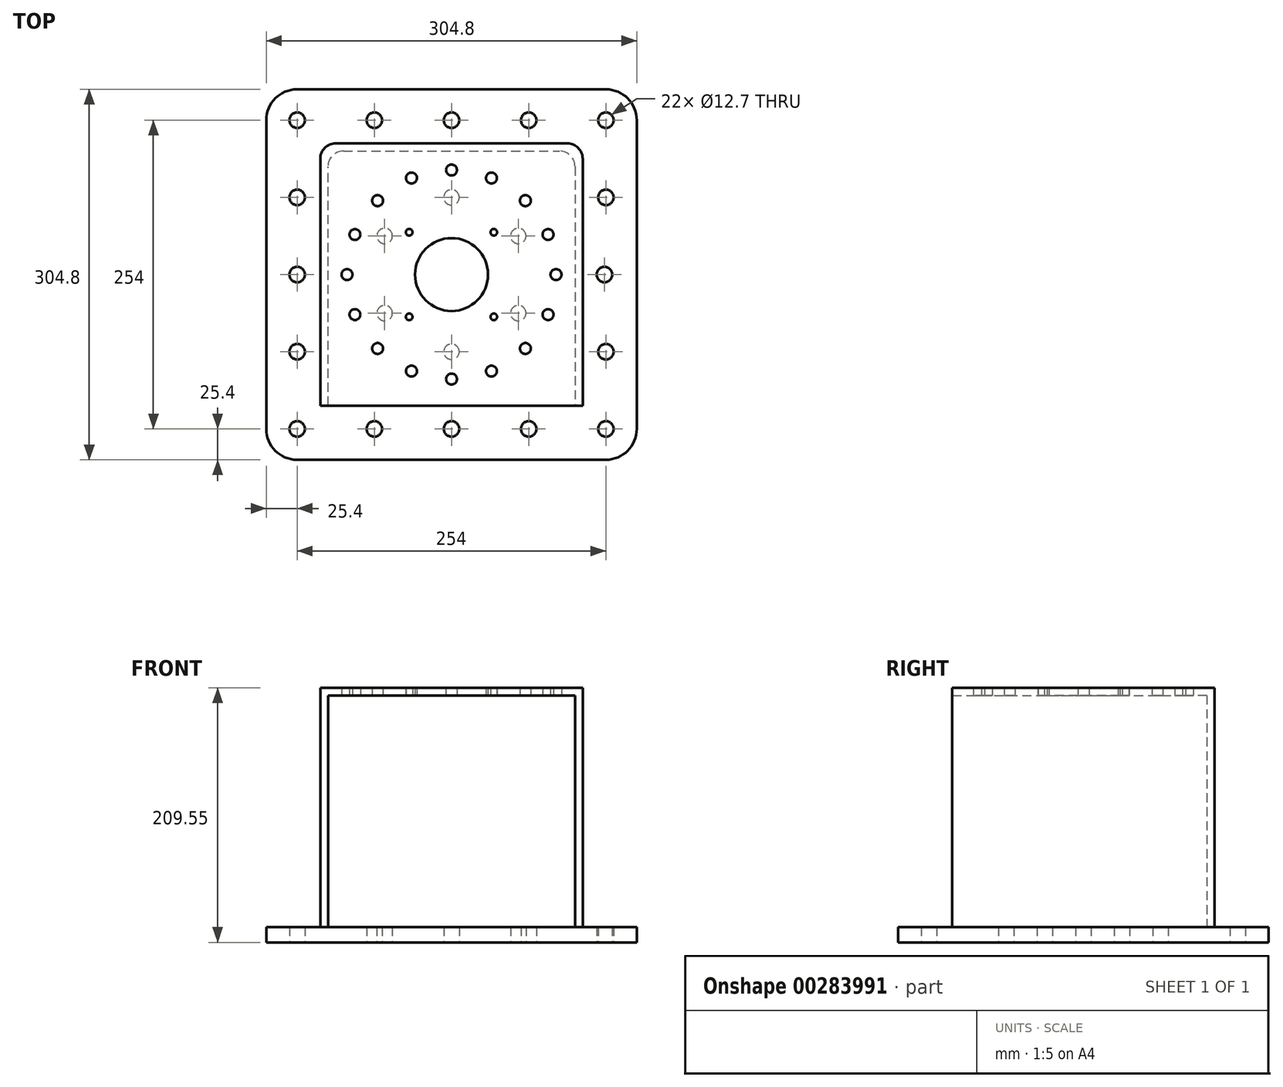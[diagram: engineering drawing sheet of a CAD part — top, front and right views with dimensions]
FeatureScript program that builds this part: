
annotation { "Feature Type Name" : "Feature", "Feature Type Description" : "" }
export const myFeature = defineFeature(function(context is Context, id is Id, definition is map)
    precondition{}
    {
        {
            var Q0;
            Q0=qCreatedBy(makeId("Top.planeOp"),FACE);
            var sketch = newSketch(context, id + "F0", { "sketchPlane" : qUnion([Q0])});
            skLineSegment(sketch, "E0.bottom", {"start": v(127, -152.4) * mm, "end": v(-127, -152.4) * mm});
            skLineSegment(sketch, "E0.top", {"start": v(127, 152.4) * mm, "end": v(-127, 152.4) * mm});
            skLineSegment(sketch, "E0.left", {"start": v(152.4, -127) * mm, "end": v(152.4, 127) * mm});
            skLineSegment(sketch, "E0.right", {"start": v(-152.4, -127) * mm, "end": v(-152.4, 127) * mm});
            skPoint(sketch, "E1.visualSharp", {"position": v(-152.4, 152.4) * mm});
            skArc(sketch, "E1.filletArc", {"start": v(-127, 152.4) * mm, "mid": v(-144.96, 144.96) * mm, "end": v(-152.4, 127) * mm});
            skPoint(sketch, "E2.visualSharp", {"position": v(152.4, 152.4) * mm});
            skArc(sketch, "E2.filletArc", {"start": v(152.4, 127) * mm, "mid": v(144.96, 144.96) * mm, "end": v(127, 152.4) * mm});
            skPoint(sketch, "E3.visualSharp", {"position": v(152.4, -152.4) * mm});
            skArc(sketch, "E3.filletArc", {"start": v(127, -152.4) * mm, "mid": v(144.96, -144.96) * mm, "end": v(152.4, -127) * mm});
            skPoint(sketch, "E4.visualSharp", {"position": v(-152.4, -152.4) * mm});
            skArc(sketch, "E4.filletArc", {"start": v(-152.4, -127) * mm, "mid": v(-144.96, -144.96) * mm, "end": v(-127, -152.4) * mm});
            skCircle(sketch, "E5", {"center": v(-127, 127) * mm, "radius": 6.35 * mm});
            skCircle(sketch, "E6.0.1.0", {"center": v(-127, -127) * mm, "radius": 6.35 * mm});
            skCircle(sketch, "E6.1.0.0", {"center": v(127, 127) * mm, "radius": 6.35 * mm});
            skCircle(sketch, "E6.1.1.0", {"center": v(127, -127) * mm, "radius": 6.35 * mm});
            skLineSegment(sketch, "E6.direction1", {"start": v(-127, 127) * mm, "end": v(127, 127) * mm, "construction": true});
            skLineSegment(sketch, "E6.direction2", {"start": v(-127, 127) * mm, "end": v(-127, -127) * mm, "construction": true});
            skCircle(sketch, "E7", {"center": v(-127, 63.5) * mm, "radius": 6.35 * mm});
            skCircle(sketch, "E8", {"center": v(-63.5, 127) * mm, "radius": 6.35 * mm});
            skCircle(sketch, "E9", {"center": v(0, 127) * mm, "radius": 6.35 * mm});
            skCircle(sketch, "E10", {"center": v(-127, 0) * mm, "radius": 6.35 * mm});
            skCircle(sketch, "E11.0.1.0", {"center": v(-127, -63.5) * mm, "radius": 6.35 * mm});
            skCircle(sketch, "E11.1.0.0", {"center": v(127, 63.5) * mm, "radius": 6.35 * mm});
            skCircle(sketch, "E11.1.1.0", {"center": v(127, -63.5) * mm, "radius": 6.35 * mm});
            skLineSegment(sketch, "E11.direction1", {"start": v(-127, 63.5) * mm, "end": v(127, 63.5) * mm, "construction": true});
            skLineSegment(sketch, "E11.direction2", {"start": v(-127, 63.5) * mm, "end": v(-127, -63.5) * mm, "construction": true});
            skCircle(sketch, "E12", {"center": v(63.5, 127) * mm, "radius": 6.35 * mm});
            skCircle(sketch, "E13", {"center": v(125.87, 0) * mm, "radius": 6.35 * mm});
            skCircle(sketch, "E14", {"center": v(-63.5, -127) * mm, "radius": 6.35 * mm});
            skCircle(sketch, "E15", {"center": v(0, -127) * mm, "radius": 6.35 * mm});
            skCircle(sketch, "E16", {"center": v(63.5, -127) * mm, "radius": 6.35 * mm});
            skLineSegment(sketch, "E17.bottom", {"start": v(107.95, -107.95) * mm, "end": v(-107.95, -107.95) * mm});
            skLineSegment(sketch, "E17.top", {"start": v(95.25, 107.95) * mm, "end": v(-95.25, 107.95) * mm});
            skLineSegment(sketch, "E17.left", {"start": v(107.95, -107.95) * mm, "end": v(107.95, 95.25) * mm});
            skLineSegment(sketch, "E17.right", {"start": v(-107.95, -107.95) * mm, "end": v(-107.95, 95.25) * mm});
            skPoint(sketch, "E17.middle", {"position": v(0, 0) * mm});
            skLineSegment(sketch, "E18", {"start": v(-101.6, -107.95) * mm, "end": v(-101.6, 88.9) * mm});
            skLineSegment(sketch, "E19", {"start": v(-88.9, 101.6) * mm, "end": v(88.9, 101.6) * mm});
            skLineSegment(sketch, "E20", {"start": v(101.6, 88.9) * mm, "end": v(101.6, -107.95) * mm});
            skPoint(sketch, "E21.visualSharp", {"position": v(-101.6, 101.6) * mm});
            skArc(sketch, "E21.filletArc", {"start": v(-88.9, 101.6) * mm, "mid": v(-97.88, 97.88) * mm, "end": v(-101.6, 88.9) * mm});
            skPoint(sketch, "E22.visualSharp", {"position": v(101.6, 101.6) * mm});
            skArc(sketch, "E22.filletArc", {"start": v(101.6, 88.9) * mm, "mid": v(97.88, 97.88) * mm, "end": v(88.9, 101.6) * mm});
            skPoint(sketch, "E23.visualSharp", {"position": v(107.95, 107.95) * mm});
            skArc(sketch, "E23.filletArc", {"start": v(107.95, 95.25) * mm, "mid": v(104.23, 104.23) * mm, "end": v(95.25, 107.95) * mm});
            skPoint(sketch, "E24.visualSharp", {"position": v(-107.95, 107.95) * mm});
            skArc(sketch, "E24.filletArc", {"start": v(-95.25, 107.95) * mm, "mid": v(-104.23, 104.23) * mm, "end": v(-107.95, 95.25) * mm});
            skCircle(sketch, "E25", {"center": v(0, 63.5) * mm, "radius": 6.35 * mm});
            skCircle(sketch, "E26.1.0", {"center": v(-55, 31.75) * mm, "radius": 6.35 * mm});
            skCircle(sketch, "E26.2.0", {"center": v(-55, -31.75) * mm, "radius": 6.35 * mm});
            skCircle(sketch, "E26.3.0", {"center": v(0, -63.5) * mm, "radius": 6.35 * mm});
            skCircle(sketch, "E26.4.0", {"center": v(55, -31.75) * mm, "radius": 6.35 * mm});
            skCircle(sketch, "E26.5.0", {"center": v(55, 31.75) * mm, "radius": 6.35 * mm});
            skSolve(sketch);
        }
        {
            var Q0;
            {var subQ0=sQuery(id+"F0.wireOp",EDGE,"E18");Q0=makeQuery(id+"F0.imprint","IMPRINT",FACE,{"disambiguationData":[TD([[makeQuery(id+"F0.imprint","IMPRINT",EDGE,{"derivedFrom":subQ0}),-1.0]])]});}
            var Q1;
            Q1=makeQuery(id+"F0.imprint","IMPRINT",FACE,{"disambiguationData":[TD([[makeQuery(id+"F0.imprint","IMPRINT",EDGE,{"derivedFrom":sQuery(id+"F0.wireOp",EDGE,"E0.bottom")}),-1.0]])]});
            extrude(context, id + "F1", {"entities" : qUnion([Q0, Q1]), "depth" : 12.7 * mm});
        }
        {
            var Q0;
            Q0=makeQuery(id+"F0.imprint","IMPRINT",FACE,{"disambiguationData":[TD([[makeQuery(id+"F0.imprint","IMPRINT",EDGE,{"derivedFrom":sQuery(id+"F0.wireOp",EDGE,"E17.top")}),1.0]])]});
            extrude(context, id + "F2", {"entities" : qUnion([Q0]), "operationType" : NewBodyOperationType.ADD, "depth" : 203.2 * mm});
        }
        {
            var Q0;
            Q0=makeQuery(id+"F2.opExtrude","CAP_FACE",FACE,{"disambiguationData":[OSD([sQuery(id+"F0.wireOp",EDGE,"E17.bottom"),sQuery(id+"F0.wireOp",EDGE,"E17.top"),sQuery(id+"F0.wireOp",EDGE,"E17.left"),sQuery(id+"F0.wireOp",EDGE,"E17.right"),sQuery(id+"F0.wireOp",EDGE,"E18"),sQuery(id+"F0.wireOp",EDGE,"E19"),sQuery(id+"F0.wireOp",EDGE,"E20"),sQuery(id+"F0.wireOp",EDGE,"E21.filletArc"),sQuery(id+"F0.wireOp",EDGE,"E22.filletArc"),sQuery(id+"F0.wireOp",EDGE,"E23.filletArc"),sQuery(id+"F0.wireOp",EDGE,"E24.filletArc")])],"isStart":false});
            var sketch = newSketch(context, id + "F3", { "sketchPlane" : qUnion([Q0])});
            skLineSegment(sketch, "E27.bottom", {"start": v(107.95, -107.95) * mm, "end": v(-107.95, -107.95) * mm});
            skLineSegment(sketch, "E27.top", {"start": v(95.25, 107.95) * mm, "end": v(-95.25, 107.95) * mm});
            skLineSegment(sketch, "E27.left", {"start": v(107.95, -107.95) * mm, "end": v(107.95, 95.25) * mm});
            skLineSegment(sketch, "E27.right", {"start": v(-107.95, -107.95) * mm, "end": v(-107.95, 95.25) * mm});
            skPoint(sketch, "E27.middle", {"position": v(0, 0) * mm});
            skPoint(sketch, "E28.visualSharp", {"position": v(-107.95, 107.95) * mm});
            skArc(sketch, "E28.filletArc", {"start": v(-95.25, 107.95) * mm, "mid": v(-104.23, 104.23) * mm, "end": v(-107.95, 95.25) * mm});
            skPoint(sketch, "E29.visualSharp", {"position": v(107.95, 107.95) * mm});
            skArc(sketch, "E29.filletArc", {"start": v(107.95, 95.25) * mm, "mid": v(104.23, 104.23) * mm, "end": v(95.25, 107.95) * mm});
            skCircle(sketch, "E30", {"center": v(0, 0) * mm, "radius": 30 * mm});
            skCircle(sketch, "E31", {"center": v(0, 0) * mm, "radius": 95 * mm});
            skCircle(sketch, "E32", {"center": v(0, 86) * mm, "radius": 4.5 * mm});
            skCircle(sketch, "E33.1.0", {"center": v(-32.91, 79.45) * mm, "radius": 4.5 * mm});
            skCircle(sketch, "E33.2.0", {"center": v(-60.81, 60.81) * mm, "radius": 4.5 * mm});
            skCircle(sketch, "E33.3.0", {"center": v(-79.45, 32.91) * mm, "radius": 4.5 * mm});
            skCircle(sketch, "E33.4.0", {"center": v(-86, 0) * mm, "radius": 4.5 * mm});
            skCircle(sketch, "E33.5.0", {"center": v(-79.45, -32.91) * mm, "radius": 4.5 * mm});
            skCircle(sketch, "E33.6.0", {"center": v(-60.81, -60.81) * mm, "radius": 4.5 * mm});
            skCircle(sketch, "E33.7.0", {"center": v(-32.91, -79.45) * mm, "radius": 4.5 * mm});
            skCircle(sketch, "E33.8.0", {"center": v(0, -86) * mm, "radius": 4.5 * mm});
            skCircle(sketch, "E33.9.0", {"center": v(32.91, -79.45) * mm, "radius": 4.5 * mm});
            skCircle(sketch, "E33.10.0", {"center": v(60.81, -60.81) * mm, "radius": 4.5 * mm});
            skCircle(sketch, "E33.11.0", {"center": v(79.45, -32.91) * mm, "radius": 4.5 * mm});
            skCircle(sketch, "E33.12.0", {"center": v(86, 0) * mm, "radius": 4.5 * mm});
            skCircle(sketch, "E33.13.0", {"center": v(79.45, 32.91) * mm, "radius": 4.5 * mm});
            skCircle(sketch, "E33.14.0", {"center": v(60.81, 60.81) * mm, "radius": 4.5 * mm});
            skCircle(sketch, "E33.15.0", {"center": v(32.91, 79.45) * mm, "radius": 4.5 * mm});
            skCircle(sketch, "E34", {"center": v(-34.8, 34.8) * mm, "radius": 2.75 * mm});
            skCircle(sketch, "E35.0.1.0", {"center": v(-34.8, -34.8) * mm, "radius": 2.75 * mm});
            skCircle(sketch, "E35.1.0.0", {"center": v(34.8, 34.8) * mm, "radius": 2.75 * mm});
            skCircle(sketch, "E35.1.1.0", {"center": v(34.8, -34.8) * mm, "radius": 2.75 * mm});
            skLineSegment(sketch, "E35.direction1", {"start": v(-34.8, 34.8) * mm, "end": v(34.8, 34.8) * mm, "construction": true});
            skLineSegment(sketch, "E35.direction2", {"start": v(-34.8, 34.8) * mm, "end": v(-34.8, -34.8) * mm, "construction": true});
            skSolve(sketch);
        }
        {
            var Q0;
            Q0=makeQuery(id+"F3.imprint","IMPRINT",FACE,{"disambiguationData":[TD([[makeQuery(id+"F3.imprint","IMPRINT",EDGE,{"derivedFrom":sQuery(id+"F3.wireOp",EDGE,"E27.top")}),1.0]])]});
            var Q1;
            Q1=makeQuery(id+"F3.imprint","IMPRINT",FACE,{"disambiguationData":[TD([[makeQuery(id+"F3.imprint","IMPRINT",EDGE,{"derivedFrom":sQuery(id+"F3.wireOp",EDGE,"E31")}),-1.0]])]});
            var Q2;
            Q2=makeQuery(id+"F3.imprint","IMPRINT",FACE,{"disambiguationData":[TD([[makeQuery(id+"F3.imprint","IMPRINT",EDGE,{"derivedFrom":sQuery(id+"F3.wireOp",EDGE,"E30")}),-1.0]])]});
            extrude(context, id + "F4", {"entities" : qUnion([Q0, Q1, Q2]), "operationType" : NewBodyOperationType.ADD, "depth" : 6.35 * mm});
        }
    });
